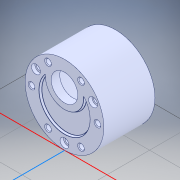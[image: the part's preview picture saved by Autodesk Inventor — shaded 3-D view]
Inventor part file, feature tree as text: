
AUTODESK INVENTOR PART (.ipt)
format: ipt  version: 2022 (Build 260153000, 153)  size: 210,944 bytes
history: native  units: mm
features: other x3, fillet x1
ambient origin geometry x8: Origin, YZ Plane, XZ Plane, XY Plane, X Axis, Y Axis, Z Axis, Center Point
bodies: Body1 (feature_tree)
feature tree (4):
  other  "Твердое тело1"
  other  "Непосредственное редактирование1"
  fillet  "Fillet1"  [1 undecoded]
  other  "Перенос1"
note: 1 required parameter value undecoded (feature->parameter linkage not recoverable at this tier; creation-order binding heuristic only, values carry confidence <= 0.55)
